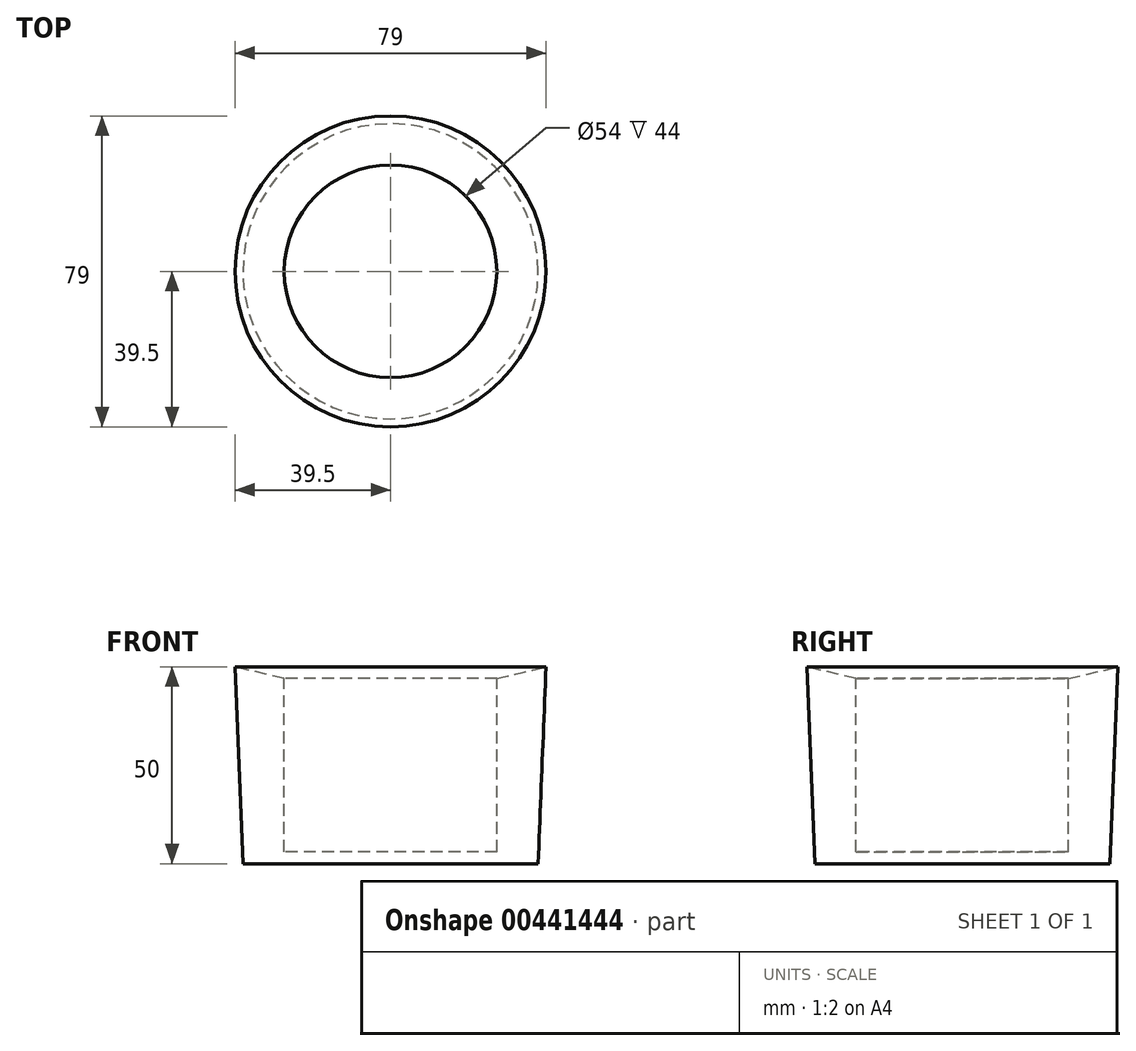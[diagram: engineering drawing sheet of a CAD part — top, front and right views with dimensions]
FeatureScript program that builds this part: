
annotation { "Feature Type Name" : "Feature", "Feature Type Description" : "" }
export const myFeature = defineFeature(function(context is Context, id is Id, definition is map)
    precondition{}
    {
        {
            var Q0;
            Q0=qCreatedBy(makeId("Front.planeOp"),FACE);
            var sketch = newSketch(context, id + "F0", { "sketchPlane" : qUnion([Q0])});
            skLineSegment(sketch, "E0", {"start": v(-39.5, 50) * mm, "end": v(-27, 47) * mm});
            skLineSegment(sketch, "E1", {"start": v(-27, 47) * mm, "end": v(-27, 3) * mm});
            skLineSegment(sketch, "E2", {"start": v(0, 3) * mm, "end": v(0, 0) * mm});
            skLineSegment(sketch, "E3", {"start": v(0, 0) * mm, "end": v(-37.5, 0) * mm});
            skLineSegment(sketch, "E4", {"start": v(-37.5, 0) * mm, "end": v(-39.5, 50) * mm});
            skLineSegment(sketch, "E5", {"start": v(0, 3) * mm, "end": v(-27, 3) * mm});
            skSolve(sketch);
        }
        {
            var Q0;
            Q0=makeQuery(id+"F0.imprint","IMPRINT",FACE,{"disambiguationData":[TD([[makeQuery(id+"F0.imprint","IMPRINT",EDGE,{"derivedFrom":sQuery(id+"F0.wireOp",EDGE,"E0")}),-1.0]])]});
            var Q1;
            Q1=sQuery(id+"F0.wireOp",EDGE,"E2");
            revolve(context, id + "F1", {"entities" : qUnion([Q0]), "axis" : qUnion([Q1]), "revolveType" : RevolveType.FULL});
        }
    });
